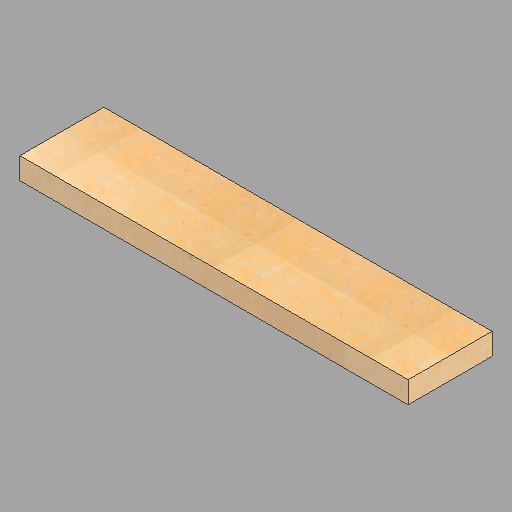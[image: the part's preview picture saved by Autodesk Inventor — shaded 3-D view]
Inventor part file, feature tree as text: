
AUTODESK INVENTOR PART (.ipt)
format: ipt  version: 2023 (Build 270158030, 158C)  size: 200,704 bytes
history: native  units: in
note: dims shown in document units (in); Inventor stores cm internally (conversion verified against a paired STEP export)
features: extrude x1, sketch x1
ambient origin geometry x8: Origin, YZ Plane, XZ Plane, XY Plane, X Axis, Y Axis, Z Axis, Center Point
bodies: Solid1 (feature_tree)
feature tree (2):
  extrude  "Extrusion1"  Depth=15.5in
  sketch  "Sketch1"  dims[d0=71.625in d1=15.5in d2=4.0in d3=0.0in]
